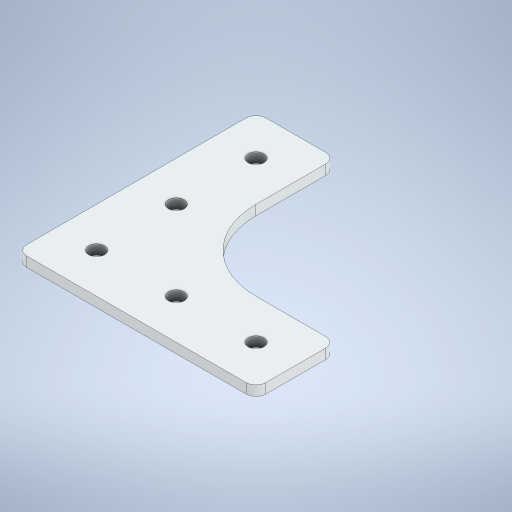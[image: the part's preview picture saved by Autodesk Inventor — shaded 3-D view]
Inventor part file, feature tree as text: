
AUTODESK INVENTOR PART (.ipt)
format: ipt  version: 2024 (Build 280153000, 153)  size: 251,392 bytes
history: native  units: in
note: dims shown in document units (in); Inventor stores cm internally (conversion verified against a paired STEP export)
features: fillet x1
ambient origin geometry x8: Origin, YZ Plane, XZ Plane, XY Plane, X Axis, Y Axis, Z Axis, Center Point
bodies: Solid1 (feature_tree)
feature tree (1):
  fillet  "Fillet1"  [1 undecoded]
note: 1 required parameter value undecoded (feature->parameter linkage not recoverable at this tier; creation-order binding heuristic only, values carry confidence <= 0.55)
